# Revit family: SS-01244_WT174M
name_source: partatom
category: Plumbing Fixtures
revit_build: Autodesk Revit 2015 (Build: 20140322_1515(x64)
units: mm (PartAtom-declared; Revit-internal decimal feet)

## types (1)
- SS-01244_WT174M
    Codes/Standards = • Meets and exceeds
o Carrier system: ASME A112.6.2
o Tank trim: IAPMO PS50, CSA B125.3, ASSE1002
• Certifications: IAPMO(cUPC), *EPA Watersense, State of Massachusetts, City of Los Angeles, and others
• Code compliance: UPC, IPC, NSPC, NPC Canada, and others
    Manufacturer = TOTO USA
    Model = WT174M
    Specifications = • Water Use 1.28GPF & 0.9GPF
(4.8LPF & 3.4LPF)
• Flush System Dual-Max
• Min. Water Pressure 8 psi (static)
• Installation Height 15" to 19" (projected range)
• Warranty One Year Limited Warranty
• Material Various
• Shipping Weight 43 lbs
• Shipping Dimensions 47-1/2" x 26" x 6"
    material = Steel, Galvanized

## geometry (parser evidence)
native form markers: Sweep x5
no freeform markers — native parametric forms only
